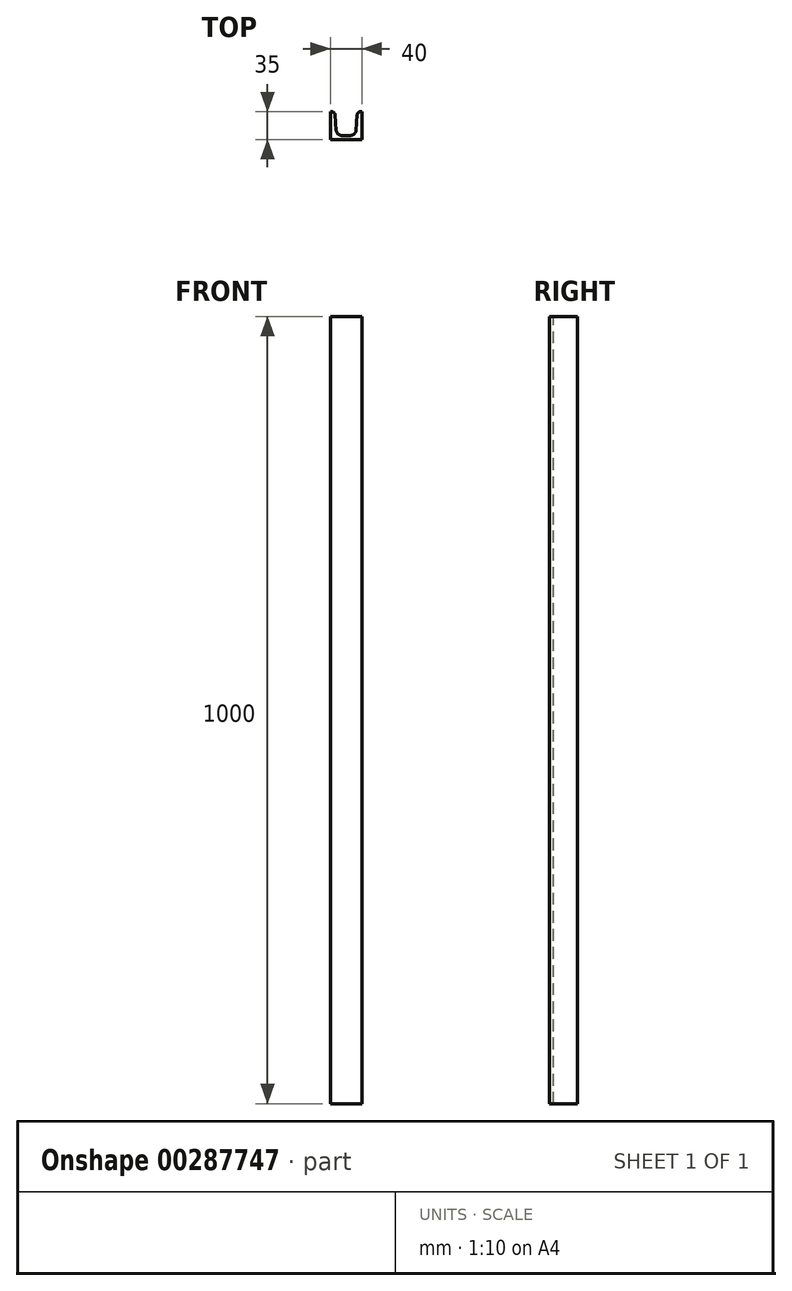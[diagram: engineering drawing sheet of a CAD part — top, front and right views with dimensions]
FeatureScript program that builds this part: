
annotation { "Feature Type Name" : "Feature", "Feature Type Description" : "" }
export const myFeature = defineFeature(function(context is Context, id is Id, definition is map)
    precondition{}
    {
        {
            var Q0;
            Q0=qCreatedBy(makeId("Top.planeOp"),FACE);
            var sketch = newSketch(context, id + "F0", { "sketchPlane" : qUnion([Q0])});
            skLineSegment(sketch, "E0.bottom", {"start": v(-20, -17.5) * mm, "end": v(20, -17.5) * mm});
            skLineSegment(sketch, "E0.top", {"start": v(-20, 17.5) * mm, "end": v(-14.4, 17.5) * mm});
            skLineSegment(sketch, "E0.left", {"start": v(-20, -17.5) * mm, "end": v(-20, 17.5) * mm});
            skLineSegment(sketch, "E0.right", {"start": v(20, -17.5) * mm, "end": v(20, 17.5) * mm});
            skLineSegment(sketch, "E1.0", {"start": v(-12, -12.5) * mm, "end": v(12, -12.5) * mm});
            skLineSegment(sketch, "E2.trimOffspring", {"start": v(14.4, 17.5) * mm, "end": v(20, 17.5) * mm});
            skLineSegment(sketch, "E3", {"start": v(-14.4, 17.5) * mm, "end": v(-12, -12.5) * mm});
            skLineSegment(sketch, "E4", {"start": v(14.4, 17.5) * mm, "end": v(12, -12.5) * mm});
            skPoint(sketch, "E5", {"position": v(-13, 0) * mm});
            skPoint(sketch, "E6", {"position": v(13, 0) * mm});
            skSolve(sketch);
        }
        {
            var Q0;
            Q0=makeQuery(id+"F0.imprint","IMPRINT",FACE,{"disambiguationData":[TD([[makeQuery(id+"F0.imprint","IMPRINT",EDGE,{"derivedFrom":sQuery(id+"F0.wireOp",EDGE,"E0.bottom")}),1.0]])]});
            extrude(context, id + "F1", {"entities" : qUnion([Q0]), "oppositeDirection" : true, "depth" : 1000 * mm});
        }
        {
            var Q0;
            Q0=makeQuery(id+"F1.opExtrude","SWEPT_EDGE",EDGE,{"disambiguationData":[OSD([sQuery(id+"F0.wireOp",EDGE,"E0.top"),sQuery(id+"F0.wireOp",EDGE,"E3")])]});
            var Q1;
            Q1=makeQuery(id+"F1.opExtrude","SWEPT_EDGE",EDGE,{"disambiguationData":[OSD([sQuery(id+"F0.wireOp",EDGE,"E2.trimOffspring"),sQuery(id+"F0.wireOp",EDGE,"E4")])]});
            fillet(context, id + "F2", {"entities" : qUnion([Q0, Q1]), "radius" : 3.5 * mm, "tangentPropagation" : true, "allowEdgeOverflow" : false});
        }
        {
            var Q0;
            Q0=makeQuery(id+"F1.opExtrude","SWEPT_EDGE",EDGE,{"disambiguationData":[OSD([sQuery(id+"F0.wireOp",EDGE,"E1.0"),sQuery(id+"F0.wireOp",EDGE,"E3")])]});
            var Q1;
            Q1=makeQuery(id+"F1.opExtrude","SWEPT_EDGE",EDGE,{"disambiguationData":[OSD([sQuery(id+"F0.wireOp",EDGE,"E1.0"),sQuery(id+"F0.wireOp",EDGE,"E4")])]});
            fillet(context, id + "F3", {"entities" : qUnion([Q0, Q1]), "radius" : 7 * mm, "tangentPropagation" : true, "allowEdgeOverflow" : false});
        }
    });
